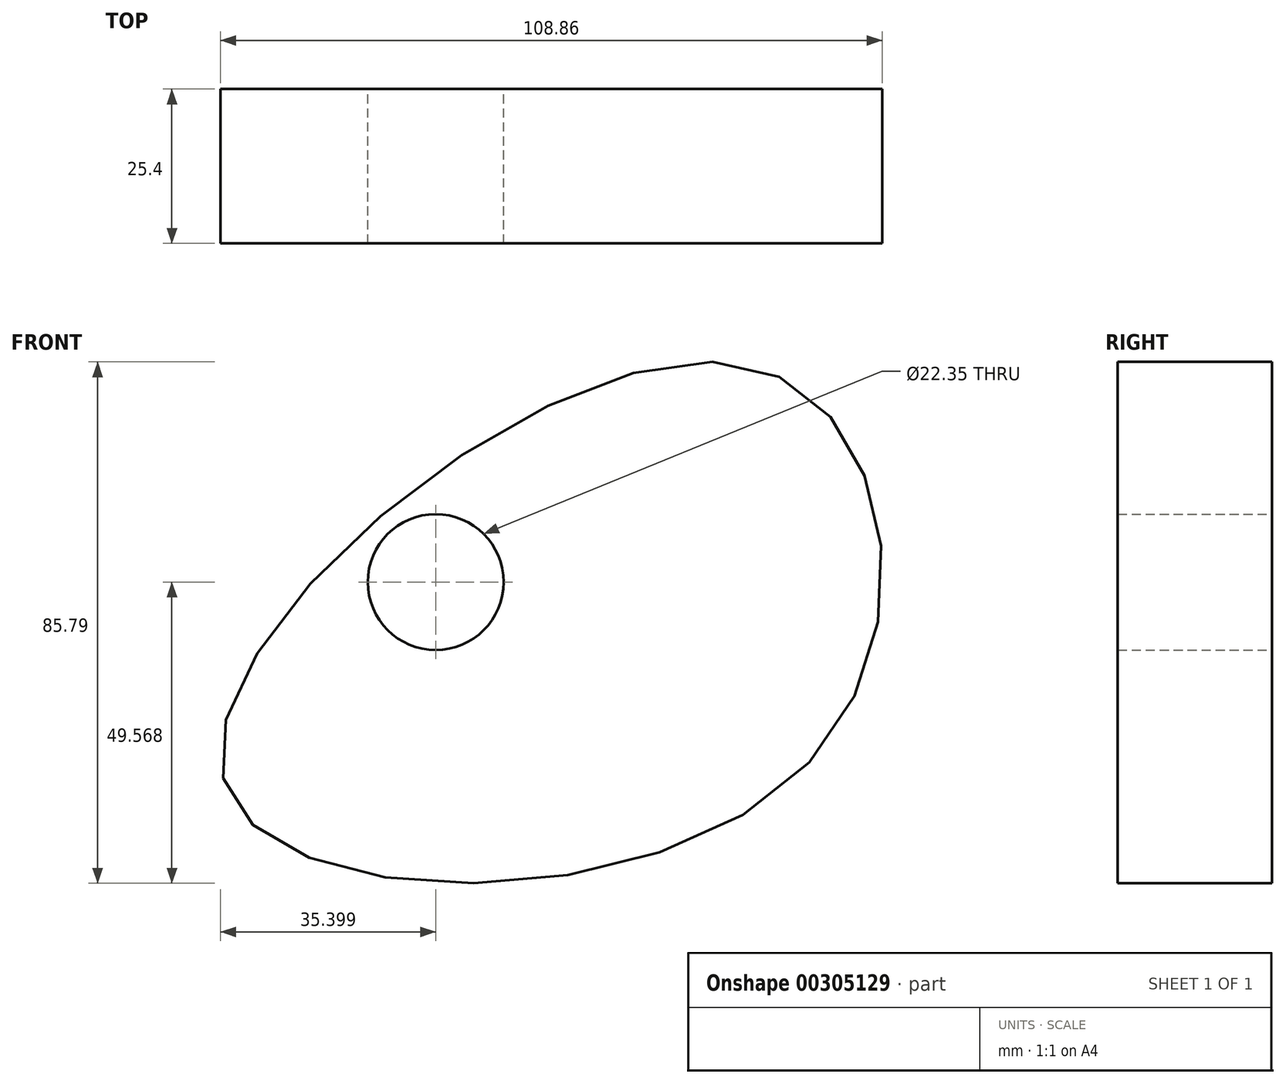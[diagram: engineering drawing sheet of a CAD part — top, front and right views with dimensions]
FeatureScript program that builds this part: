
annotation { "Feature Type Name" : "Feature", "Feature Type Description" : "" }
export const myFeature = defineFeature(function(context is Context, id is Id, definition is map)
    precondition{}
    {
        {
            var Q0;
            Q0=qCreatedBy(makeId("Front.planeOp"),FACE);
            var sketch = newSketch(context, id + "F0", { "sketchPlane" : qUnion([Q0])});
            skFitSpline(sketch, "E0", {"points": [v(-55.65, -15.94) * mm, v(40, -14.14) * mm, v(30.31, 51.98) * mm, v(-55.65, -15.94) * mm]});
            skCircle(sketch, "E1", {"center": v(-20.7, 16.36) * mm, "radius": 11.17 * mm});
            skSolve(sketch);
        }
        {
            var Q0;
            Q0 = qSketchRegion(id + "F0", true);
            extrude(context, id + "F1", {"entities" : qUnion([Q0]), "depth" : 25.4 * mm});
        }
    });
